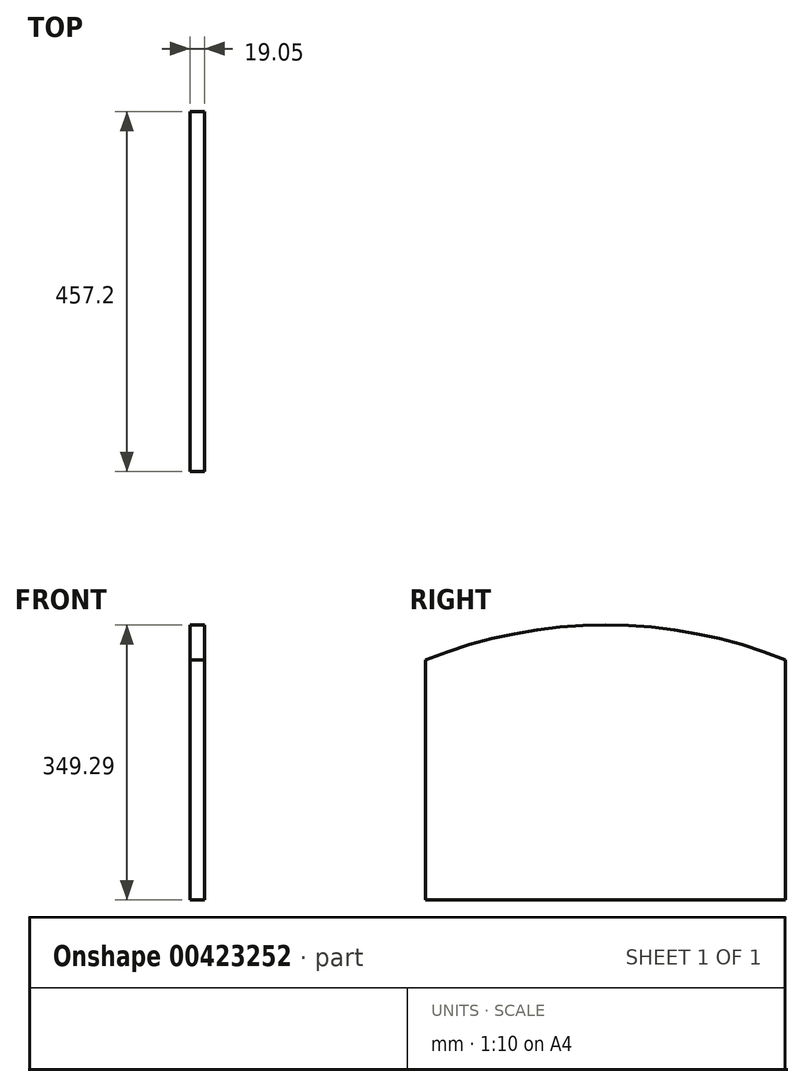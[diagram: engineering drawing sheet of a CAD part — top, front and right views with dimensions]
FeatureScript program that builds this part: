
annotation { "Feature Type Name" : "Feature", "Feature Type Description" : "" }
export const myFeature = defineFeature(function(context is Context, id is Id, definition is map)
    precondition{}
    {
        {
            var Q0;
            Q0=qCreatedBy(makeId("Right.planeOp"),FACE);
            var sketch = newSketch(context, id + "F0", { "sketchPlane" : qUnion([Q0])});
            skLineSegment(sketch, "E0.top", {"start": v(249.96, -135.84) * mm, "end": v(-207.24, -135.84) * mm});
            skLineSegment(sketch, "E0.left", {"start": v(249.96, 168.96) * mm, "end": v(249.96, -135.84) * mm});
            skLineSegment(sketch, "E0.right", {"start": v(-207.24, 168.96) * mm, "end": v(-207.24, -135.84) * mm});
            skArc(sketch, "E1", {"start": v(249.96, 168.96) * mm, "mid": v(21.36, 213.45) * mm, "end": v(-207.24, 168.96) * mm});
            skSolve(sketch);
        }
        {
            var Q0;
            Q0=makeQuery(id+"F0.imprint","IMPRINT",FACE,{"disambiguationData":[TD([[makeQuery(id+"F0.imprint","IMPRINT",EDGE,{"derivedFrom":sQuery(id+"F0.wireOp",EDGE,"E0.top")}),-1.0]])]});
            extrude(context, id + "F1", {"entities" : qUnion([Q0]), "depth" : 19.05 * mm, "offsetDistance" : 25.4 * mm});
        }
    });
